# Revit family: ToiletRollHolder_SurfaceMount_Abey_Vela
name_source: partatom
category: Specialty Equipment
units: mm (PartAtom-declared; Revit-internal decimal feet)

## family parameters
Always vertical = Yes
Cut with Voids When Loaded = No
OmniClass Number = 23.31.25.21
OmniClass Title = Toilet Paper Dispensers
Part Type = Normal
Room Calculation Point = No
Round Connector Dimension = Use Diameter
Shared = No
Work Plane-Based = No

## types (5) — shared parameters
Assembly Code = C1030210
IfcExportAs = IfcFurniture
IfcExportType = NOTDEFINED
Manufacturer = Abey
ManufacturerOverallDepth = 65 mm  [stored 0.213255 ft]
ManufacturerOverallHeight = 29 mm  [stored 0.0951444 ft]
ManufacturerOverallWidth = 145 mm  [stored 0.475722 ft]
ManufacturerURLProductSpecific = https://www.abey.com.au
ModifiedIssue = 20241025 $
URL = https://www.abey.com.au
Uniclass2015Code = Pr_40_70_22_61
Uniclass2015Title = Paper roll dispensers
Uniclass2015Version = Products v1.33
zero-valued in all types: Default Elevation

## per-type parameters (varying)
| type | Description | ManufacturerSpecCode | Material | Model | Type Comments |
| Chrome (VTRH) | Vela Toilet Roll Holder Chrome | VTRH | Metal_Abey_Chrome | VTRH | Chrome |
| Black (VTRH-B) | Vela Toilet Roll Holder Black | VTRH-B | Metal_Abey_Black | VTRH-B | Black |
| Brushed Brass (VTRH-BB) | Vela Toilet Roll Holder Brushed Brass | VTRH-BB | Metal_Abey_Brass | VTRH-BB | Brushed Brass |
| Gun Metal (VTRH-GM) | Vela Toilet Roll Holder Gun Metal | VTRH-GM | Metal_Abey_GunMetal | VTRH-GM | Gun Metal |
| Brushed Nickel (VTRH-BN) | Vela Toilet Roll Holder Brushed Nickel | VTRH-BN | Metal_Abey_BrushedNickel | VTRH-BN | Brushed Nickel |

note: [stored X ft] marks values corroborated as IEEE doubles in the binary element streams (Revit-internal decimal feet)

## geometry (parser evidence)
native form markers: Sweep x2
no freeform markers — native parametric forms only
